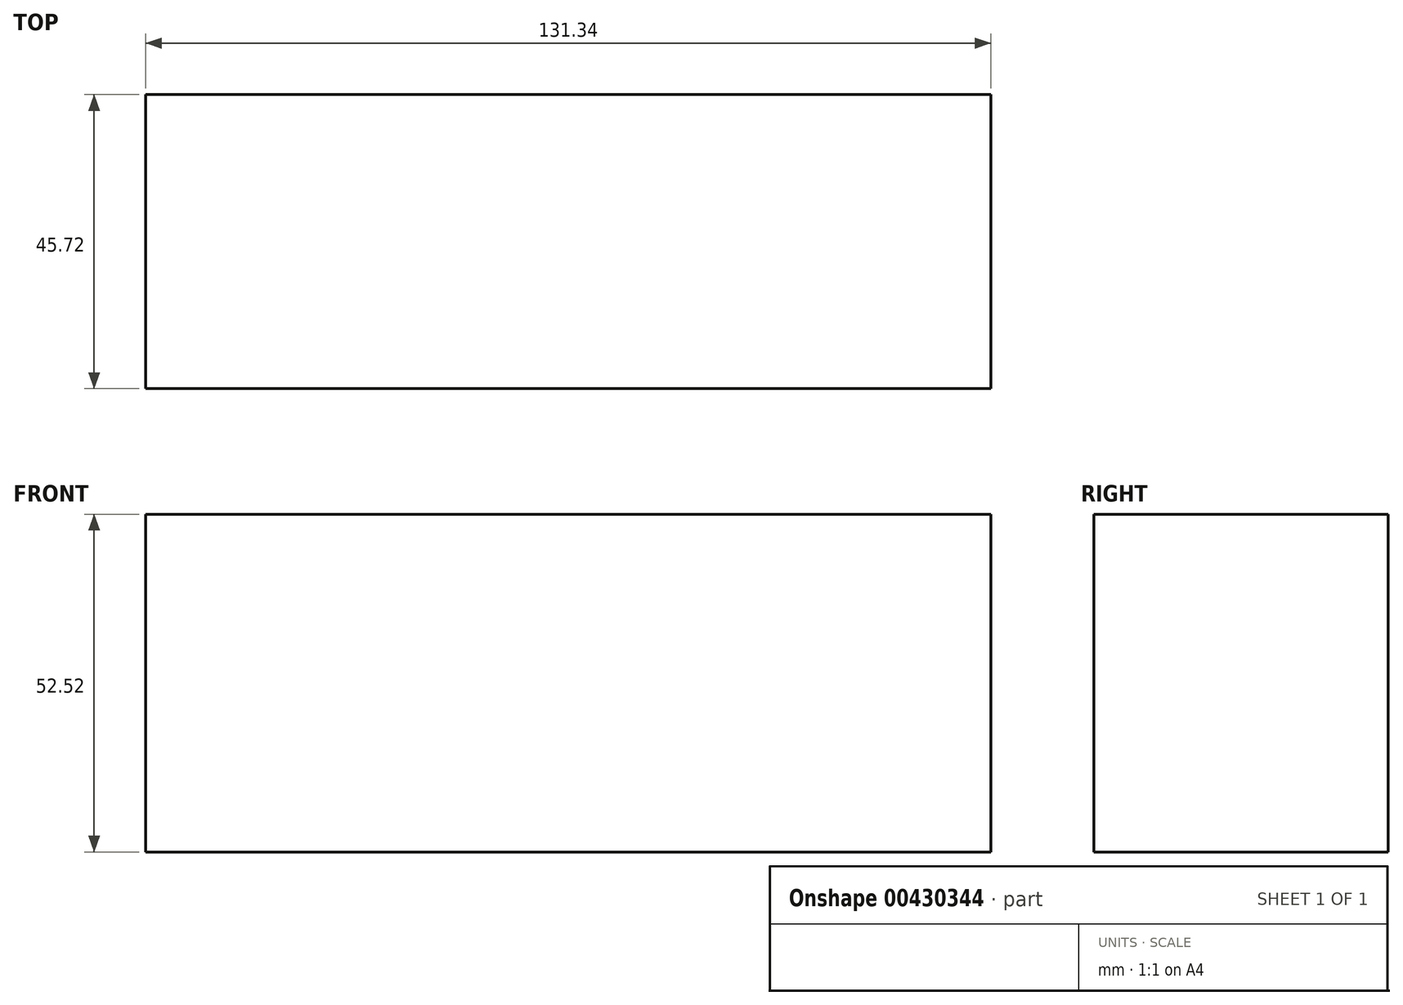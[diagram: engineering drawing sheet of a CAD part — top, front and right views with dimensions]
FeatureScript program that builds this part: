
annotation { "Feature Type Name" : "Feature", "Feature Type Description" : "" }
export const myFeature = defineFeature(function(context is Context, id is Id, definition is map)
    precondition{}
    {
        {
            var Q0;
            Q0=qCreatedBy(makeId("Front.planeOp"),FACE);
            var sketch = newSketch(context, id + "F0", { "sketchPlane" : qUnion([Q0])});
            skLineSegment(sketch, "E0.bottom", {"start": v(51.57, -26.26) * mm, "end": v(-51.57, -26.26) * mm});
            skLineSegment(sketch, "E0.top", {"start": v(51.57, 26.26) * mm, "end": v(-51.57, 26.26) * mm});
            skLineSegment(sketch, "E0.left", {"start": v(51.57, -26.26) * mm, "end": v(51.57, 26.26) * mm});
            skLineSegment(sketch, "E0.right", {"start": v(-51.57, -26.26) * mm, "end": v(-51.57, 26.26) * mm});
            skPoint(sketch, "E0.middle", {"position": v(0, 0) * mm});
            skSolve(sketch);
        }
        {
            var Q0;
            Q0=makeQuery(id+"F0.imprint","IMPRINT",FACE,{"disambiguationData":[TD([[makeQuery(id+"F0.imprint","IMPRINT",EDGE,{"derivedFrom":sQuery(id+"F0.wireOp",EDGE,"E0.bottom")}),-1.0]])]});
            extrude(context, id + "F1", {"entities" : qUnion([Q0]), "depth" : 45.72 * mm});
        }
        {
            var Q0;
            Q0=makeQuery(id+"F1.opExtrude","SWEPT_FACE",FACE,{"disambiguationData":[OSD([sQuery(id+"F0.wireOp",EDGE,"E0.right")])]});
            extrude(context, id + "F2", {"entities" : qUnion([Q0]), "operationType" : NewBodyOperationType.ADD, "depth" : 28.2 * mm});
        }
    });
